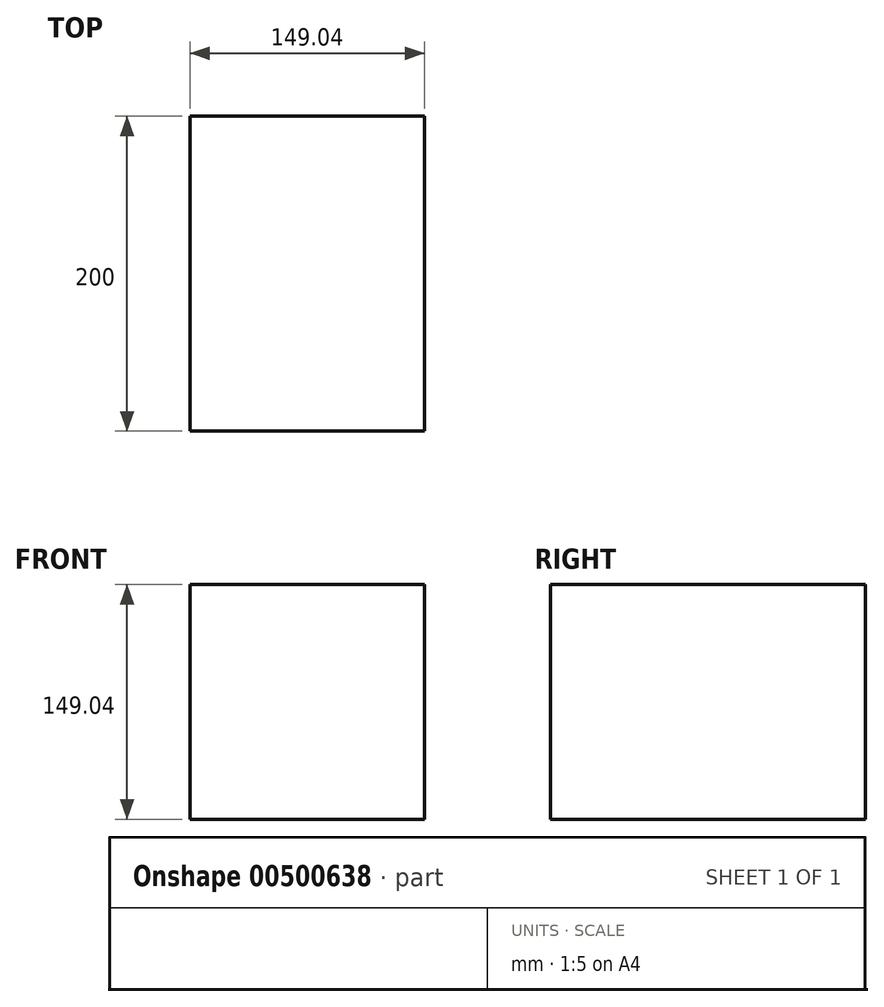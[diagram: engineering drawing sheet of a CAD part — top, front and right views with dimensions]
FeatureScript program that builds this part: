
annotation { "Feature Type Name" : "Feature", "Feature Type Description" : "" }
export const myFeature = defineFeature(function(context is Context, id is Id, definition is map)
    precondition{}
    {
        {
            var Q0;
            Q0=qCreatedBy(makeId("Front.planeOp"),FACE);
            var sketch = newSketch(context, id + "F0", { "sketchPlane" : qUnion([Q0])});
            skCircle(sketch, "E0.cCircle", {"center": v(0, 0) * mm, "radius": 105.39 * mm, "construction": true});
            skLineSegment(sketch, "E0.0", {"start": v(74.52, 74.52) * mm, "end": v(74.52, -74.52) * mm});
            skLineSegment(sketch, "E0.1", {"start": v(74.52, -74.52) * mm, "end": v(-74.52, -74.52) * mm});
            skLineSegment(sketch, "E0.2", {"start": v(-74.52, -74.52) * mm, "end": v(-74.52, 74.52) * mm});
            skLineSegment(sketch, "E0.3", {"start": v(-74.52, 74.52) * mm, "end": v(74.52, 74.52) * mm});
            skSolve(sketch);
        }
        {
            var Q0;
            Q0=makeQuery(id+"F0.imprint","IMPRINT",FACE,{"disambiguationData":[TD([[makeQuery(id+"F0.imprint","IMPRINT",EDGE,{"derivedFrom":sQuery(id+"F0.wireOp",EDGE,"E0.0")}),-1.0]])]});
            extrude(context, id + "F1", {"entities" : qUnion([Q0]), "depth" : 200 * mm});
        }
    });
